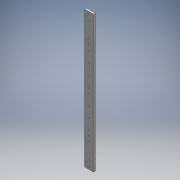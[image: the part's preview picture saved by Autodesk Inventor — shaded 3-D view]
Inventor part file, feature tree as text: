
AUTODESK INVENTOR PART (.ipt)
format: ipt  version: 2016 (Build 200138000, 138)  size: 140,288 bytes
history: native  units: mm
features: reference x21, extrude x1, sketch x1
ambient origin geometry x8: Origin, YZ Plane, XZ Plane, XY Plane, X Axis, Y Axis, Z Axis, Center Point
bodies: Body1 (feature_tree)
feature tree (23):
  extrude  "Extrusion6"  Depth=416.0mm
  sketch  "Sketch1"  dims[d0=27.0mm d1=416.0mm d14=8.0mm d15=5.5mm d16=13.5mm d17=16.0mm d18=80.0mm d19=16.0mm d20=80.0mm d21=16.0mm d22=5.5mm d23=5.5mm d24=8.0mm d25=13.5mm d26=16.0mm d27=16.0mm d28=16.0mm d29=32.0mm d30=32.0mm d31=32.0mm d32=16.0mm d33=32.0mm d34=32.0mm d35=32.0mm d36=16.0mm d37=16.0mm d38=48.0mm d39=48.0mm d40=5.5mm d41=6.0mm d42=0.0mm]
  reference  "Reference1"
  reference  "Reference2"
  reference  "Reference5"
  reference  "Reference6"
  reference  "Reference7"
  reference  "Reference9"
  reference  "Reference11"
  reference  "Reference15"
  reference  "Reference16"
  reference  "Reference17"
  reference  "Reference19"
  reference  "Reference21"
  reference  "Reference23"
  reference  "Reference24"
  reference  "Reference25"
  reference  "Reference28"
  reference  "Reference29"
  reference  "Reference31"
  reference  "Reference32"
  reference  "Reference35"
  reference  "Reference37"
